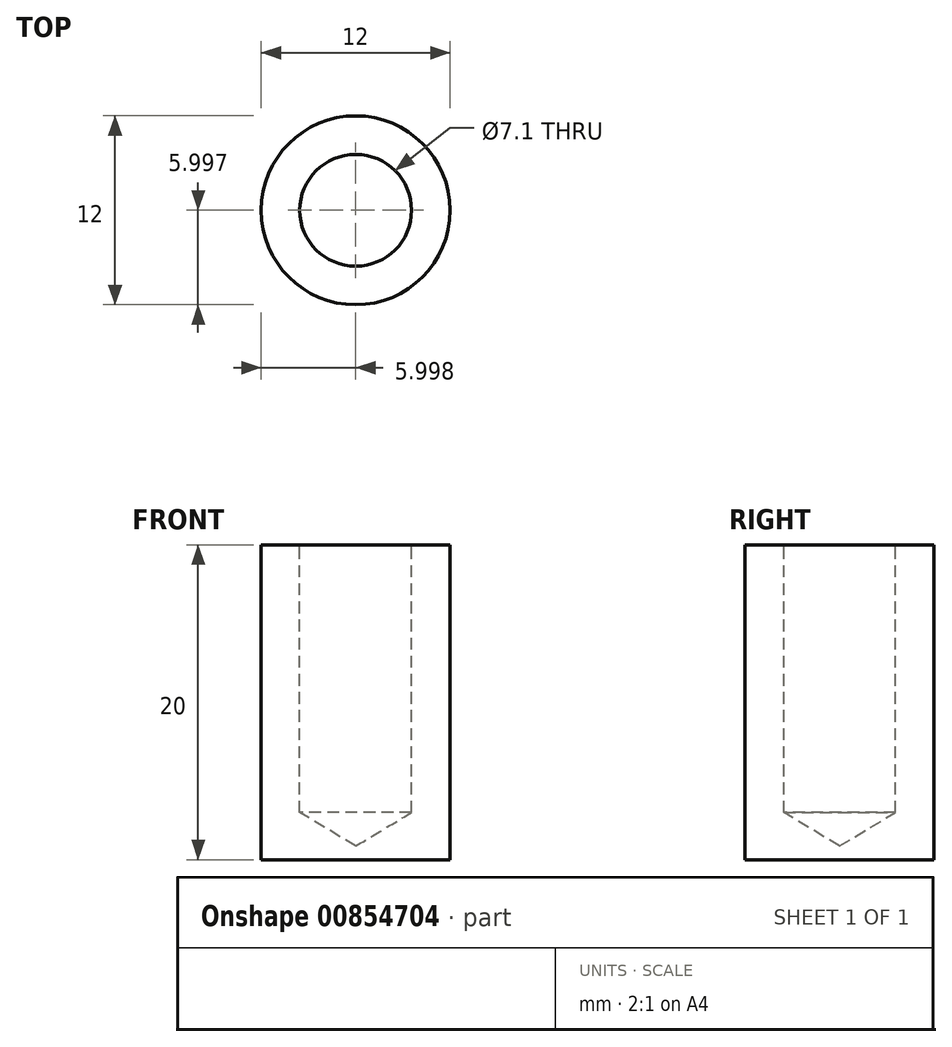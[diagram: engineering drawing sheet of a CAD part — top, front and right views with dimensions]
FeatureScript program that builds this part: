
annotation { "Feature Type Name" : "Feature", "Feature Type Description" : "" }
export const myFeature = defineFeature(function(context is Context, id is Id, definition is map)
    precondition{}
    {
        {
            var Q0;
            Q0=qCreatedBy(makeId("Top.planeOp"),FACE);
            var sketch = newSketch(context, id + "F0", { "sketchPlane" : qUnion([Q0])});
            skCircle(sketch, "E0", {"center": v(-44.5, 22.29) * mm, "radius": 6 * mm});
            skSolve(sketch);
        }
        {
            var Q0;
            Q0=makeQuery(id+"F0.imprint","IMPRINT",FACE,{"disambiguationData":[TD([[makeQuery(id+"F0.imprint","IMPRINT",EDGE,{"derivedFrom":sQuery(id+"F0.wireOp",EDGE,"E0")}),1.0]])]});
            extrude(context, id + "F1", {"entities" : qUnion([Q0]), "depth" : 20 * mm, "offsetDistance" : 25 * mm});
        }
        {
            var Q0;
            Q0=makeQuery(id+"F1.opExtrude","CAP_FACE",FACE,{"disambiguationData":[OSD([sQuery(id+"F0.wireOp",EDGE,"E0")])],"isStart":false});
            var sketch = newSketch(context, id + "F2", { "sketchPlane" : qUnion([Q0])});
            skLineSegment(sketch, "E1", {"start": v(-44.5, 22.29) * mm, "end": v(-42.07, 27.77) * mm, "construction": true});
            skSolve(sketch);
        }
        {
            var Q0;
            Q0=sQuery(id+"F2.wireOp",VERTEX,"E1.start");
            var Q1;
            Q1=makeQuery(id+"F1.opExtrude","SWEPT_BODY",BODY,{"disambiguationData":[OSD([sQuery(id+"F0.wireOp",EDGE,"E0")])]});
            hole(context, id + "F3", {"style" : HoleStyle.SIMPLE, "endStyle" : HoleEndStyle.BLIND, "holeDiameter" : 7.1 * mm, "majorDiameter" : 5 * mm, "holeDepth" : 17 * mm, "isTappedThrough" : true, "tappedDepth" : 12 * mm, "tapClearance" : 3, "locations" : qUnion([Q0]), "scope" : qUnion([Q1])});
        }
    });
